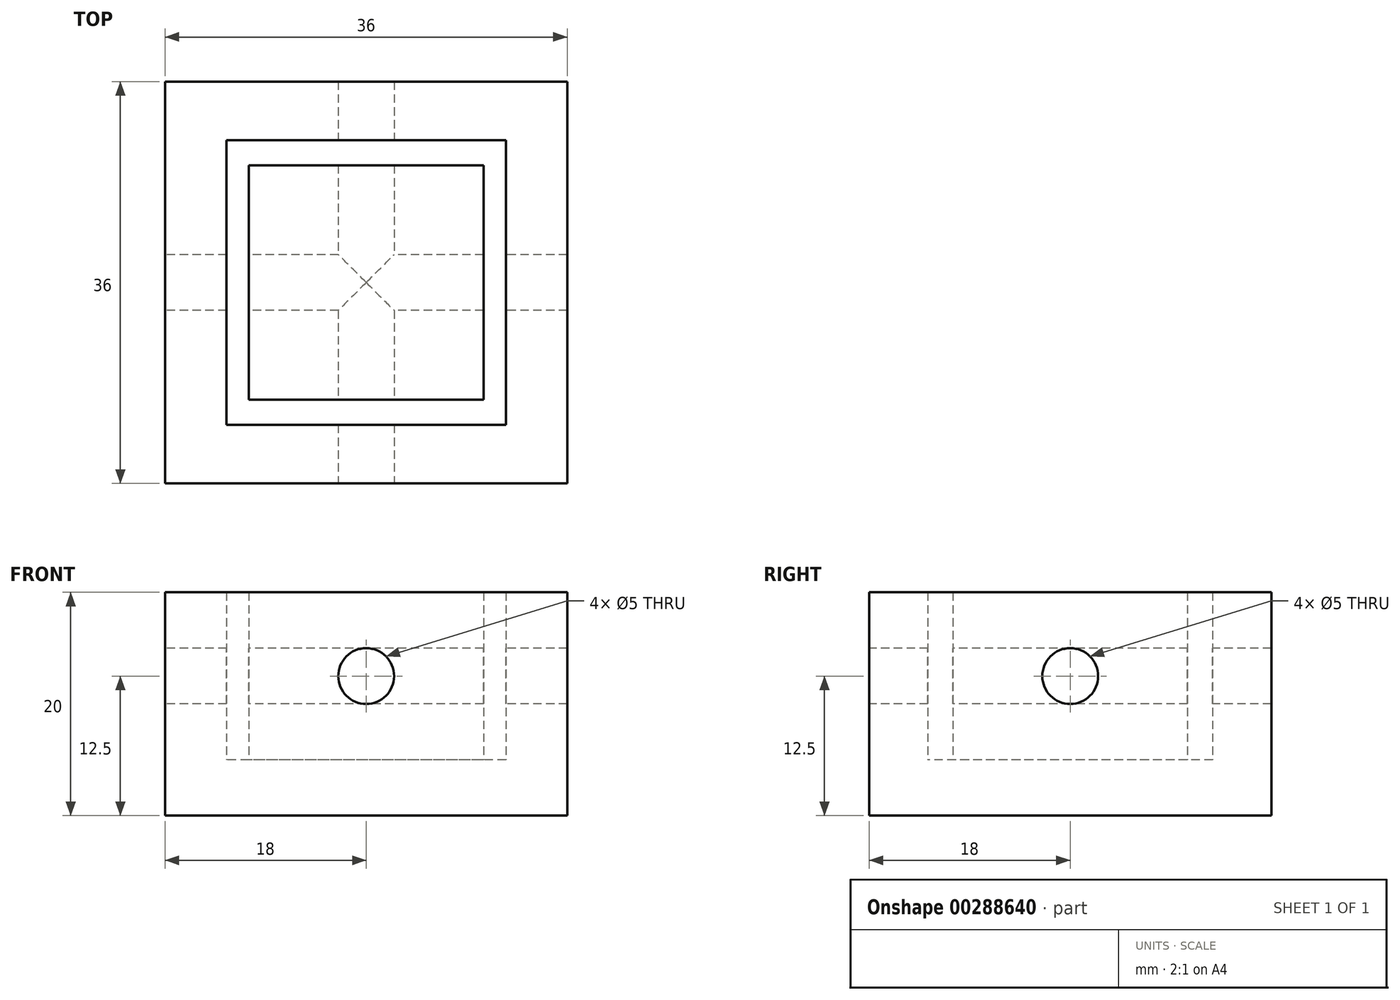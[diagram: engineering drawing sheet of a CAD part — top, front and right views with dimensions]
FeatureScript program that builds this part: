
annotation { "Feature Type Name" : "Feature", "Feature Type Description" : "" }
export const myFeature = defineFeature(function(context is Context, id is Id, definition is map)
    precondition{}
    {
        {
            var Q0;
            Q0=qCreatedBy(makeId("Top.planeOp"),FACE);
            var sketch = newSketch(context, id + "F0", { "sketchPlane" : qUnion([Q0])});
            skLineSegment(sketch, "E0.bottom", {"start": v(18, 18) * mm, "end": v(-18, 18) * mm});
            skLineSegment(sketch, "E0.top", {"start": v(18, -18) * mm, "end": v(-18, -18) * mm});
            skLineSegment(sketch, "E0.left", {"start": v(18, 18) * mm, "end": v(18, -18) * mm});
            skLineSegment(sketch, "E0.right", {"start": v(-18, 18) * mm, "end": v(-18, -18) * mm});
            skPoint(sketch, "E0.middle", {"position": v(0, 0) * mm});
            skSolve(sketch);
        }
        {
            var Q0;
            Q0 = qSketchRegion(id + "F0", true);
            extrude(context, id + "F1", {"entities" : qUnion([Q0]), "depth" : 5 * mm});
        }
        {
            var Q0;
            Q0=makeQuery(id+"F1.opExtrude","CAP_FACE",FACE,{"disambiguationData":[OSD([sQuery(id+"F0.wireOp",EDGE,"E0.bottom"),sQuery(id+"F0.wireOp",EDGE,"E0.top"),sQuery(id+"F0.wireOp",EDGE,"E0.left"),sQuery(id+"F0.wireOp",EDGE,"E0.right")])],"isStart":false});
            var sketch = newSketch(context, id + "F2", { "sketchPlane" : qUnion([Q0])});
            skLineSegment(sketch, "E1.bottom", {"start": v(10.5, 10.5) * mm, "end": v(-10.5, 10.5) * mm});
            skLineSegment(sketch, "E1.top", {"start": v(10.5, -10.5) * mm, "end": v(-10.5, -10.5) * mm});
            skLineSegment(sketch, "E1.left", {"start": v(10.5, 10.5) * mm, "end": v(10.5, -10.5) * mm});
            skLineSegment(sketch, "E1.right", {"start": v(-10.5, 10.5) * mm, "end": v(-10.5, -10.5) * mm});
            skPoint(sketch, "E1.middle", {"position": v(0, 0) * mm});
            skSolve(sketch);
        }
        {
            var Q0;
            Q0=makeQuery(id+"F2.imprint","IMPRINT",FACE,{"disambiguationData":[TD([[makeQuery(id+"F2.imprint","IMPRINT",EDGE,{"derivedFrom":sQuery(id+"F2.wireOp",EDGE,"E1.bottom")}),1.0]])]});
            extrude(context, id + "F3", {"entities" : qUnion([Q0]), "operationType" : NewBodyOperationType.ADD, "depth" : 15 * mm});
        }
        {
            var Q0;
            Q0=makeQuery(id+"F1.opExtrude","CAP_FACE",FACE,{"disambiguationData":[OSD([sQuery(id+"F0.wireOp",EDGE,"E0.bottom"),sQuery(id+"F0.wireOp",EDGE,"E0.top"),sQuery(id+"F0.wireOp",EDGE,"E0.left"),sQuery(id+"F0.wireOp",EDGE,"E0.right")])],"isStart":false});
            var sketch = newSketch(context, id + "F4", { "sketchPlane" : qUnion([Q0])});
            skLineSegment(sketch, "E2.bottom", {"start": v(12.5, 12.74) * mm, "end": v(-12.5, 12.74) * mm});
            skLineSegment(sketch, "E2.top", {"start": v(12.5, -12.74) * mm, "end": v(-12.5, -12.74) * mm});
            skLineSegment(sketch, "E2.left", {"start": v(12.5, 12.74) * mm, "end": v(12.5, -12.74) * mm});
            skLineSegment(sketch, "E2.right", {"start": v(-12.5, 12.74) * mm, "end": v(-12.5, -12.74) * mm});
            skPoint(sketch, "E2.middle", {"position": v(0, 0) * mm});
            skSolve(sketch);
        }
        {
            var Q0;
            Q0=makeQuery(id+"F4.imprint","IMPRINT",FACE,{"disambiguationData":[TD([[makeQuery(id+"F4.imprint","IMPRINT",EDGE,{"derivedFrom":sQuery(id+"F4.wireOp",EDGE,"E2.bottom")}),-1.0]])]});
            extrude(context, id + "F5", {"entities" : qUnion([Q0]), "operationType" : NewBodyOperationType.ADD, "depth" : 15 * mm});
        }
        {
            var Q0;
            {var subQ0=sQuery(id+"F0.wireOp",EDGE,"E0.top");Q0=makeQuery(id+"F5.boolean.opBoolean","MERGE",FACE,{"derivedFrom":[makeQuery(id+"F1.opExtrude","SWEPT_FACE",FACE,{"disambiguationData":[OSD([subQ0])]}),makeQuery(id+"F5.opExtrude","SWEPT_FACE",FACE,{"disambiguationData":[OSD([subQ0])]})]});}
            var sketch = newSketch(context, id + "F6", { "sketchPlane" : qUnion([Q0])});
            skCircle(sketch, "E3", {"center": v(0, 12.5) * mm, "radius": 2.5 * mm});
            skPoint(sketch, "E3.centerSnap0", {"position": v(0, 0) * mm});
            skSolve(sketch);
        }
        {
            var Q0;
            Q0=makeQuery(id+"F6.imprint","IMPRINT",FACE,{"disambiguationData":[TD([[makeQuery(id+"F6.imprint","IMPRINT",EDGE,{"derivedFrom":sQuery(id+"F6.wireOp",EDGE,"E3")}),1.0]])]});
            extrude(context, id + "F7", {"entities" : qUnion([Q0]), "operationType" : NewBodyOperationType.REMOVE, "oppositeDirection" : true, "depth" : 40 * mm, "offsetDistance" : 25 * mm});
        }
        {
            var Q0;
            {var subQ0=sQuery(id+"F0.wireOp",EDGE,"E0.right");Q0=makeQuery(id+"F5.boolean.opBoolean","MERGE",FACE,{"derivedFrom":[makeQuery(id+"F1.opExtrude","SWEPT_FACE",FACE,{"disambiguationData":[OSD([subQ0])]}),makeQuery(id+"F5.opExtrude","SWEPT_FACE",FACE,{"disambiguationData":[OSD([subQ0])]})]});}
            var sketch = newSketch(context, id + "F8", { "sketchPlane" : qUnion([Q0])});
            skCircle(sketch, "E4", {"center": v(0, 12.5) * mm, "radius": 2.5 * mm});
            skSolve(sketch);
        }
        {
            var Q0;
            Q0=makeQuery(id+"F8.imprint","IMPRINT",FACE,{"disambiguationData":[TD([[makeQuery(id+"F8.imprint","IMPRINT",EDGE,{"derivedFrom":sQuery(id+"F8.wireOp",EDGE,"E4")}),1.0]])]});
            extrude(context, id + "F9", {"entities" : qUnion([Q0]), "operationType" : NewBodyOperationType.REMOVE, "oppositeDirection" : true, "depth" : 40 * mm, "offsetDistance" : 25 * mm});
        }
    });
